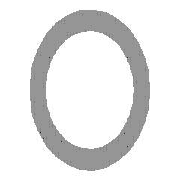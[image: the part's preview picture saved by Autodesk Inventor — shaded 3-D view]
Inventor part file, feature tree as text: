
AUTODESK INVENTOR PART (.ipt)
format: ipt  version: 2021 (Build 250183000, 183)  size: 119,808 bytes
history: native  units: mm (DEFAULTED — no unit token found)
features: other x5, plane x2, sketch x2, sweep x1
ambient origin geometry x8: Origin, YZ Plane, XZ Plane, XY Plane, X Axis, Y Axis, Z Axis, Center Point
bodies: Solid1 (feature_tree)
feature tree (10):
  parser-record x1  (decoder bookkeeping rows leaked as tree rows — omitted from the tree; the rows remain in map.json)
  other  "Driven Length"
  other  "Plano inicial"
  other  "Plano final"
  other  "Trayectoria de barrido"
  plane  "Plano de trabajo de orientación"
  sweep  "Cuerpo"
  sketch  "Sketch3"  dims[d0=60.452mm d1=3.9116mm]
  plane  "Work Plane3"
  sketch  "Sketch4"  dims[d4=-0.0mm d5=60.0mm d6=90.0deg d7=60.0mm d8=0.0mm d9=0.0mm]
